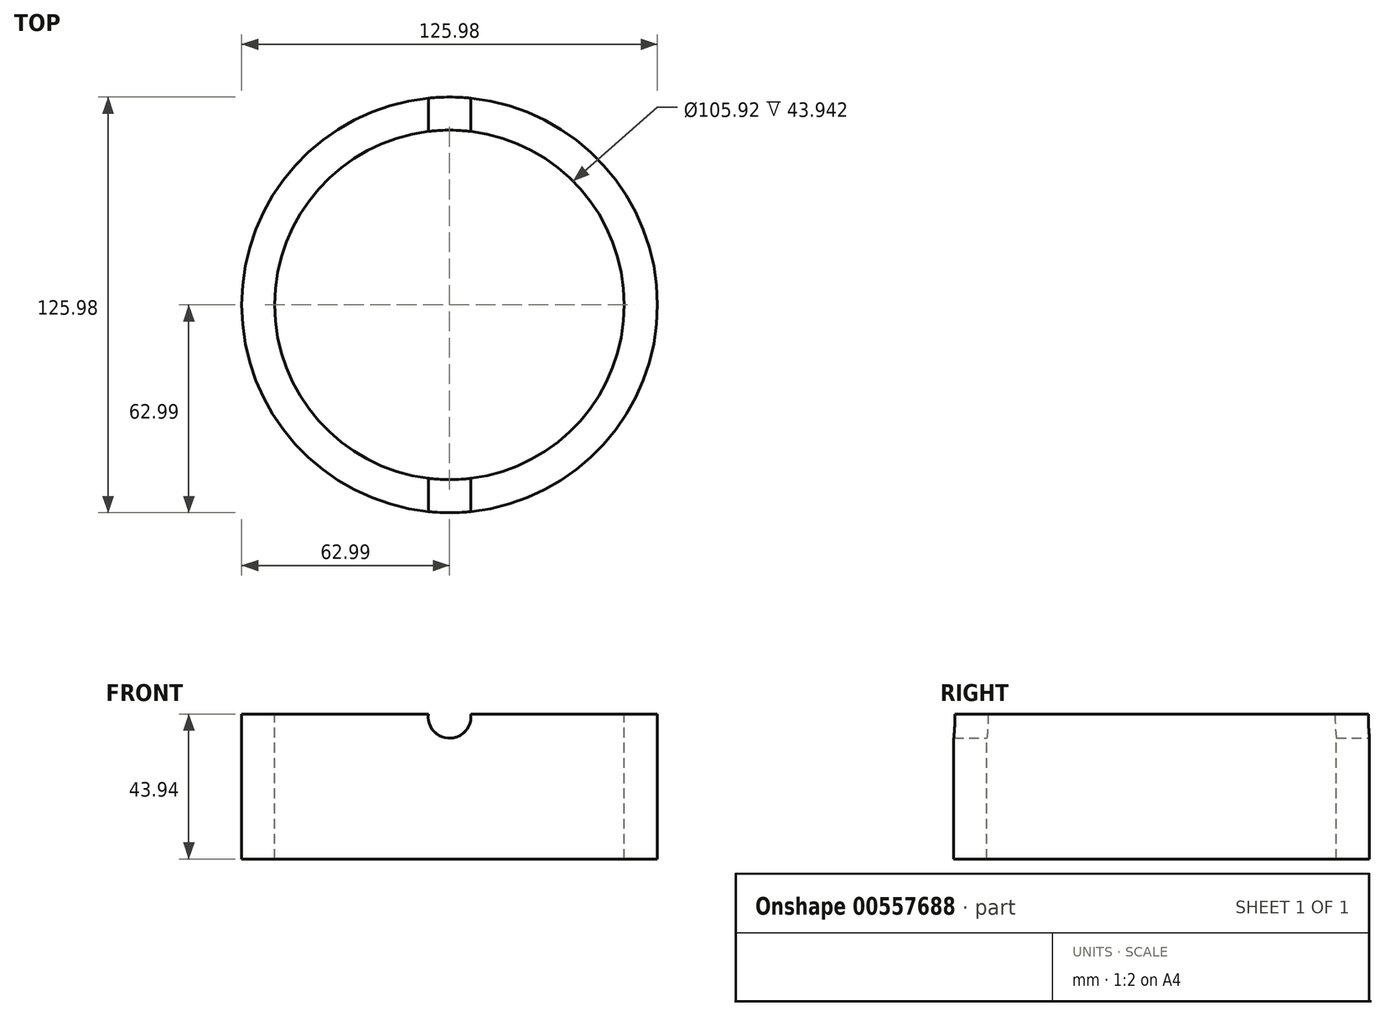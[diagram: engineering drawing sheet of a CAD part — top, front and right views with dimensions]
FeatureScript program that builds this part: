
annotation { "Feature Type Name" : "Feature", "Feature Type Description" : "" }
export const myFeature = defineFeature(function(context is Context, id is Id, definition is map)
    precondition{}
    {
        {
            var Q0;
            Q0=qCreatedBy(makeId("Top.planeOp"),FACE);
            var sketch = newSketch(context, id + "F0", { "sketchPlane" : qUnion([Q0])});
            skCircle(sketch, "E0", {"center": v(0, 0) * mm, "radius": 63 * mm});
            skSolve(sketch);
        }
        {
            var Q0;
            Q0 = qSketchRegion(id + "F0", true);
            extrude(context, id + "F1", {"entities" : qUnion([Q0]), "depth" : 43.94 * mm, "offsetDistance" : 25.4 * mm});
        }
        {
            var Q0;
            Q0=makeQuery(id+"F1.opExtrude","CAP_FACE",FACE,{"disambiguationData":[OSD([sQuery(id+"F0.wireOp",EDGE,"E0")])],"isStart":false});
            var sketch = newSketch(context, id + "F2", { "sketchPlane" : qUnion([Q0])});
            skCircle(sketch, "E1", {"center": v(0, 0) * mm, "radius": 52.96 * mm});
            skSolve(sketch);
        }
        {
            var Q0;
            Q0=makeQuery(id+"F2.imprint","IMPRINT",FACE,{"disambiguationData":[TD([[makeQuery(id+"F2.imprint","IMPRINT",EDGE,{"derivedFrom":sQuery(id+"F2.wireOp",EDGE,"E1")}),1.0]])]});
            extrude(context, id + "F3", {"entities" : qUnion([Q0]), "operationType" : NewBodyOperationType.REMOVE, "oppositeDirection" : true, "depth" : 43.94 * mm, "offsetDistance" : 25.4 * mm});
        }
        {
            var Q0;
            Q0=qCreatedBy(makeId("Front.planeOp"),FACE);
            var sketch = newSketch(context, id + "F4", { "sketchPlane" : qUnion([Q0])});
            skCircle(sketch, "E2", {"center": v(0, 43.1) * mm, "radius": 6.49 * mm});
            skSolve(sketch);
        }
        {
            var Q0;
            Q0 = qSketchRegion(id + "F4", true);
            extrude(context, id + "F5", {"entities" : qUnion([Q0]), "operationType" : NewBodyOperationType.REMOVE, "endBound" : BoundingType.SYMMETRIC, "depth" : 127 * mm, "offsetDistance" : 25.4 * mm});
        }
    });
